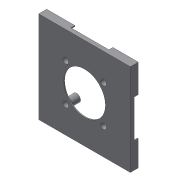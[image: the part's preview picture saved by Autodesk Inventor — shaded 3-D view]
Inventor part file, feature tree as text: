
AUTODESK INVENTOR PART (.ipt)
format: ipt  version: 2017 (Build 210142000, 142)  size: 290,816 bytes
history: native  units: mm
features: sketch x9, extrude x7, projected_geometry x3, pattern_circular x2, hole x1, fillet x1
ambient origin geometry x8: Origin, YZ Plane, XZ Plane, XY Plane, X Axis, Y Axis, Z Axis, Center Point
bodies: Solid1 (feature_tree)
feature tree (23):
  extrude  "Extrusion1"  Depth=90.0mm
  sketch  "Sketch2"  dims[d2=92.0mm d3=92.0mm]
  extrude  "Extrusion2"  Depth=92.0mm
  extrude  "Extrusion3"  Depth=90.0mm
  hole  "Hole1"  [1 undecoded]
  pattern_circular  "Circular Pattern2"  [2 undecoded]
  extrude  "Extrusion4"  Depth=2.0mm
  extrude  "Extrusion5"  Depth=2.0mm
  extrude  "Extrusion6"  Depth=10.0mm TaperAngle=0.0deg
  extrude  "Extrusion7"  Depth=2.0mm
  fillet  "Fillet1"  Radius=27.0mm
  pattern_circular  "Circular Pattern3"  Count=4 Angle=360.0deg
  sketch  "Sketch1"  dims[d0=90.0mm d1=90.0mm]
  projected_geometry  "Projected Loop1"
  sketch  "Sketch3"  dims[d4=1.0mm d5=0.0mm d6=90.0mm]
  sketch  "Sketch4"  dims[d7=90.0mm d8=1.0mm]
  projected_geometry  "Projected Loop2"
  projected_geometry  "Projected Loop3"
  sketch  "Sketch5"  dims[d9=1.0mm]
  sketch  "Sketch6"  dims[d10=10.0mm]
  sketch  "Sketch7"  dims[d11=10.0mm]
  sketch  "Sketch8"  dims[d12=14.5mm]
  sketch  "Sketch9"  dims[d13=17.25mm d14=7.0mm d15=0.0mm d16=22.5mm d17=8.625mm d18=10.0mm d19=0.0mm d23=27.0mm d24=27.0mm d25=4.0mm d26=6.0mm d27=4.0mm d28=2.0mm d29=90.0deg d30=8.0mm d31=20.594885mm d32=40.0mm d33=360.0deg d35=42.0mm d36=10.0mm d37=0.0mm d38=90.0mm d39=90.0mm d40=3.0mm d41=0.0mm d42=8.0mm d43=10.0mm d44=0.0mm d45=6.0mm d46=10.0mm d47=0.0mm d48=2.0mm d49=40.0mm d50=360.0deg]
note: 3 required parameter values undecoded (feature->parameter linkage not recoverable at this tier; creation-order binding heuristic only, values carry confidence <= 0.55)
